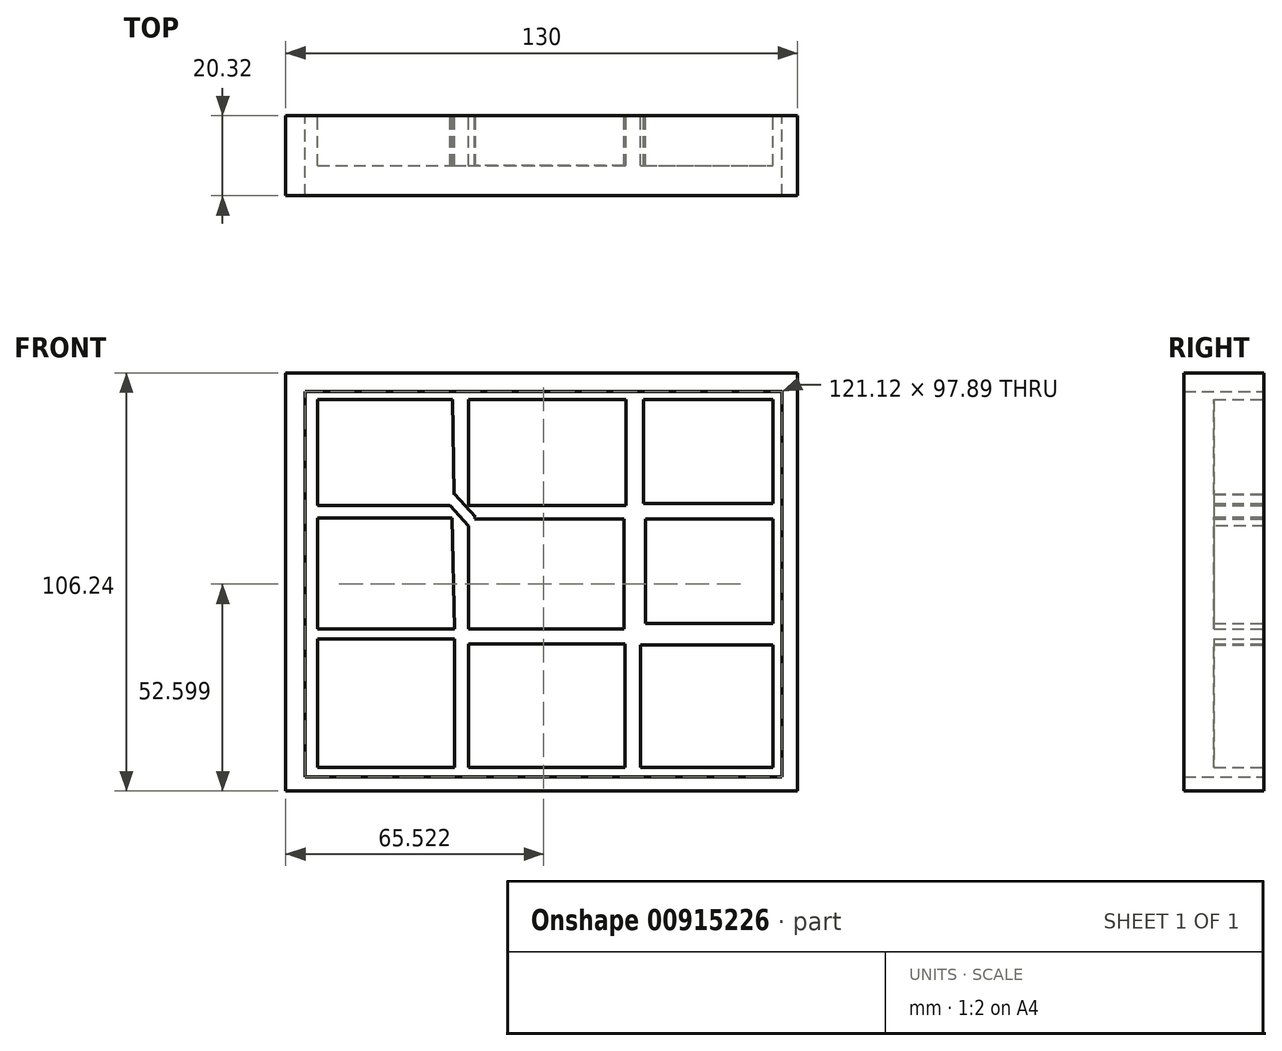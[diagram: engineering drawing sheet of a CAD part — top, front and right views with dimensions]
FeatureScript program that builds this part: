
annotation { "Feature Type Name" : "Feature", "Feature Type Description" : "" }
export const myFeature = defineFeature(function(context is Context, id is Id, definition is map)
    precondition{}
    {
        {
            var Q0;
            Q0=qCreatedBy(makeId("Front.planeOp"),FACE);
            var sketch = newSketch(context, id + "F0", { "sketchPlane" : qUnion([Q0])});
            skLineSegment(sketch, "E0.bottom", {"start": v(-56.9, 49.08) * mm, "end": v(58.73, 49.08) * mm});
            skLineSegment(sketch, "E0.top", {"start": v(-56.9, -44.38) * mm, "end": v(58.73, -44.38) * mm});
            skLineSegment(sketch, "E0.left", {"start": v(-56.9, 49.08) * mm, "end": v(-56.9, -44.38) * mm});
            skLineSegment(sketch, "E0.right", {"start": v(58.73, 49.08) * mm, "end": v(58.73, -44.38) * mm});
            skLineSegment(sketch, "E1", {"start": v(-56.9, -11.75) * mm, "end": v(-22.19, -11.75) * mm});
            skLineSegment(sketch, "E2", {"start": v(-56.9, 22.19) * mm, "end": v(-22.19, 22.19) * mm});
            skLineSegment(sketch, "E3", {"start": v(-56.9, -9.14) * mm, "end": v(-22.19, -9.14) * mm});
            skLineSegment(sketch, "E4", {"start": v(-22.19, -11.75) * mm, "end": v(-22.19, -44.38) * mm});
            skLineSegment(sketch, "E5", {"start": v(-22.19, -9.14) * mm, "end": v(-18.53, -9.14) * mm});
            skLineSegment(sketch, "E6", {"start": v(-18.53, -44.38) * mm, "end": v(-18.53, -9.14) * mm});
            skLineSegment(sketch, "E7", {"start": v(-56.9, 19.06) * mm, "end": v(-22.71, 19.06) * mm});
            skLineSegment(sketch, "E8", {"start": v(-22.71, 19.06) * mm, "end": v(-22.19, -9.14) * mm});
            skLineSegment(sketch, "E9", {"start": v(-22.19, 22.19) * mm, "end": v(-18.53, 22.19) * mm});
            skLineSegment(sketch, "E10", {"start": v(-18.53, 22.19) * mm, "end": v(-18.53, -9.14) * mm});
            skLineSegment(sketch, "E11", {"start": v(-22.19, 22.19) * mm, "end": v(-22.71, 50.38) * mm});
            skLineSegment(sketch, "E12", {"start": v(-22.71, 50.38) * mm, "end": v(-18.53, 49.08) * mm});
            skLineSegment(sketch, "E13", {"start": v(-18.53, 49.08) * mm, "end": v(-18.53, 22.19) * mm});
            skLineSegment(sketch, "E14", {"start": v(-18.53, -9.14) * mm, "end": v(20.88, -9.14) * mm});
            skLineSegment(sketch, "E15", {"start": v(20.88, -9.14) * mm, "end": v(20.88, 18.8) * mm});
            skLineSegment(sketch, "E16", {"start": v(20.88, 18.8) * mm, "end": v(-18.53, 18.8) * mm});
            skLineSegment(sketch, "E17", {"start": v(-18.53, 22.19) * mm, "end": v(21.4, 22.19) * mm});
            skLineSegment(sketch, "E18", {"start": v(21.4, 22.19) * mm, "end": v(21.4, 49.08) * mm});
            skLineSegment(sketch, "E19", {"start": v(-18.53, -13.05) * mm, "end": v(21.14, -13.05) * mm});
            skLineSegment(sketch, "E20", {"start": v(21.14, -13.05) * mm, "end": v(21.14, -44.38) * mm});
            skLineSegment(sketch, "E21", {"start": v(25.06, -44.38) * mm, "end": v(25.06, -13.31) * mm});
            skLineSegment(sketch, "E22", {"start": v(25.06, -13.31) * mm, "end": v(58.73, -13.31) * mm});
            skLineSegment(sketch, "E23", {"start": v(58.73, -7.83) * mm, "end": v(26.37, -7.83) * mm});
            skLineSegment(sketch, "E24", {"start": v(26.37, -7.83) * mm, "end": v(26.37, 18.8) * mm});
            skLineSegment(sketch, "E25", {"start": v(26.37, 18.8) * mm, "end": v(58.73, 18.8) * mm});
            skLineSegment(sketch, "E26", {"start": v(25.84, 49.08) * mm, "end": v(25.84, 22.71) * mm});
            skLineSegment(sketch, "E27", {"start": v(25.84, 22.71) * mm, "end": v(58.73, 22.71) * mm});
            skSolve(sketch);
        }
        {
            var Q0;
            {var subQ5=sQuery(id+"F0.wireOp",EDGE,"E2");Q0=makeQuery(id+"F0.imprint","IMPRINT",FACE,{"disambiguationData":[TD([[makeQuery(id+"F0.imprint","IMPRINT",EDGE,{"derivedFrom":subQ5}),1.0]])]});}
            var Q1;
            {var subQ0=sQuery(id+"F0.wireOp",EDGE,"E13");Q1=makeQuery(id+"F0.imprint","IMPRINT",FACE,{"disambiguationData":[TD([[makeQuery(id+"F0.imprint","IMPRINT",EDGE,{"derivedFrom":subQ0}),1.0]])]});}
            var Q2;
            {var subQ3=sQuery(id+"F0.wireOp",EDGE,"E26");Q2=makeQuery(id+"F0.imprint","IMPRINT",FACE,{"disambiguationData":[TD([[makeQuery(id+"F0.imprint","IMPRINT",EDGE,{"derivedFrom":subQ3}),1.0]])]});}
            var Q3;
            {var subQ0=sQuery(id+"F0.wireOp",EDGE,"E3");Q3=makeQuery(id+"F0.imprint","IMPRINT",FACE,{"disambiguationData":[TD([[makeQuery(id+"F0.imprint","IMPRINT",EDGE,{"derivedFrom":subQ0}),1.0]])]});}
            var Q4;
            {var subQ0=sQuery(id+"F0.wireOp",EDGE,"E14");Q4=makeQuery(id+"F0.imprint","IMPRINT",FACE,{"disambiguationData":[TD([[makeQuery(id+"F0.imprint","IMPRINT",EDGE,{"derivedFrom":subQ0}),1.0]])]});}
            var Q5;
            {var subQ0=sQuery(id+"F0.wireOp",EDGE,"E23");Q5=makeQuery(id+"F0.imprint","IMPRINT",FACE,{"disambiguationData":[TD([[makeQuery(id+"F0.imprint","IMPRINT",EDGE,{"derivedFrom":subQ0}),-1.0]])]});}
            var Q6;
            {var subQ4=sQuery(id+"F0.wireOp",EDGE,"E1");Q6=makeQuery(id+"F0.imprint","IMPRINT",FACE,{"disambiguationData":[TD([[makeQuery(id+"F0.imprint","IMPRINT",EDGE,{"derivedFrom":subQ4}),-1.0]])]});}
            var Q7;
            {var subQ4=sQuery(id+"F0.wireOp",EDGE,"E19");Q7=makeQuery(id+"F0.imprint","IMPRINT",FACE,{"disambiguationData":[TD([[makeQuery(id+"F0.imprint","IMPRINT",EDGE,{"derivedFrom":subQ4}),-1.0]])]});}
            var Q8;
            {var subQ3=sQuery(id+"F0.wireOp",EDGE,"E21");Q8=makeQuery(id+"F0.imprint","IMPRINT",FACE,{"disambiguationData":[TD([[makeQuery(id+"F0.imprint","IMPRINT",EDGE,{"derivedFrom":subQ3}),-1.0]])]});}
            extrude(context, id + "F1", {"entities" : qUnion([Q0, Q1, Q2, Q3, Q4, Q5, Q6, Q7, Q8]), "depth" : 12.7 * mm, "offsetDistance" : 25.4 * mm});
        }
        {
            var Q0;
            Q0=qCreatedBy(makeId("Front.planeOp"),FACE);
            var sketch = newSketch(context, id + "F2", { "sketchPlane" : qUnion([Q0])});
            skLineSegment(sketch, "E28.bottom", {"start": v(-65, 55.86) * mm, "end": v(65, 55.86) * mm});
            skLineSegment(sketch, "E28.top", {"start": v(-65, -50.38) * mm, "end": v(65, -50.38) * mm});
            skLineSegment(sketch, "E28.left", {"start": v(-65, 55.86) * mm, "end": v(-65, -50.38) * mm});
            skLineSegment(sketch, "E28.right", {"start": v(65, 55.86) * mm, "end": v(65, -50.38) * mm});
            skLineSegment(sketch, "E29.bottom", {"start": v(-60.04, 51.16) * mm, "end": v(61.08, 51.16) * mm});
            skLineSegment(sketch, "E29.top", {"start": v(-60.04, -46.73) * mm, "end": v(61.08, -46.73) * mm});
            skLineSegment(sketch, "E29.left", {"start": v(-60.04, 51.16) * mm, "end": v(-60.04, -46.73) * mm});
            skLineSegment(sketch, "E29.right", {"start": v(61.08, 51.16) * mm, "end": v(61.08, -46.73) * mm});
            skSolve(sketch);
        }
        {
            var Q0;
            Q0=makeQuery(id+"F2.imprint","IMPRINT",FACE,{"disambiguationData":[TD([[makeQuery(id+"F2.imprint","IMPRINT",EDGE,{"derivedFrom":sQuery(id+"F2.wireOp",EDGE,"E28.bottom")}),-1.0]])]});
            extrude(context, id + "F3", {"entities" : qUnion([Q0]), "depth" : 20.32 * mm, "offsetDistance" : 25.4 * mm});
        }
        {
            var Q0;
            Q0=qCreatedBy(makeId("Front.planeOp"),FACE);
            var sketch = newSketch(context, id + "F4", { "sketchPlane" : qUnion([Q0])});
            skLineSegment(sketch, "E30", {"start": v(-24.02, 22.97) * mm, "end": v(-18.27, 16.7) * mm});
            skLineSegment(sketch, "E31", {"start": v(-22.19, 25.06) * mm, "end": v(-16.84, 19.22) * mm});
            skLineSegment(sketch, "E32", {"start": v(-24.02, 22.97) * mm, "end": v(-22.19, 25.06) * mm});
            skLineSegment(sketch, "E33", {"start": v(-18.27, 16.7) * mm, "end": v(-16.84, 19.22) * mm});
            skSolve(sketch);
        }
        {
            var Q0;
            Q0=makeQuery(id+"F4.imprint","IMPRINT",FACE,{"disambiguationData":[TD([[makeQuery(id+"F4.imprint","IMPRINT",EDGE,{"derivedFrom":sQuery(id+"F4.wireOp",EDGE,"E30")}),1.0]])]});
            extrude(context, id + "F5", {"entities" : qUnion([Q0]), "operationType" : NewBodyOperationType.ADD, "depth" : 12.7 * mm, "offsetDistance" : 25.4 * mm});
        }
    });
